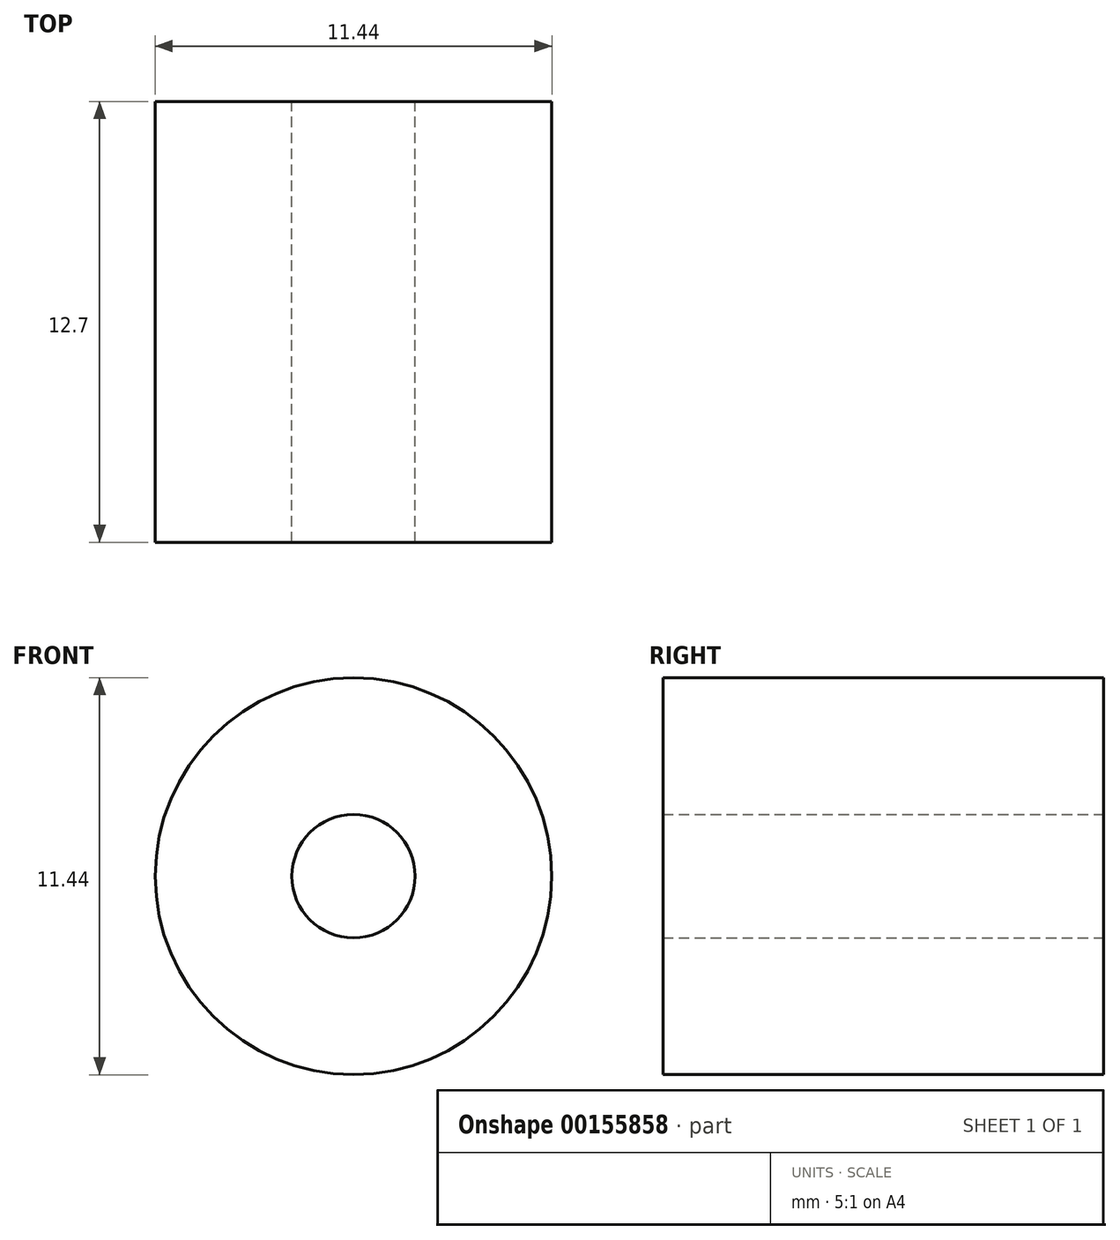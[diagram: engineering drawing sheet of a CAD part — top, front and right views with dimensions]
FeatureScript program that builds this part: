
annotation { "Feature Type Name" : "Feature", "Feature Type Description" : "" }
export const myFeature = defineFeature(function(context is Context, id is Id, definition is map)
    precondition{}
    {
        {
            var Q0;
            Q0=qCreatedBy(makeId("Front.planeOp"),FACE);
            var sketch = newSketch(context, id + "F0", { "sketchPlane" : qUnion([Q0])});
            skCircle(sketch, "E0", {"center": v(0, 0) * mm, "radius": 1.78 * mm});
            skCircle(sketch, "E1", {"center": v(0, 0) * mm, "radius": 5.72 * mm});
            skSolve(sketch);
        }
        {
            var Q0;
            Q0=makeQuery(id+"F0.imprint","IMPRINT",FACE,{"disambiguationData":[TD([[makeQuery(id+"F0.imprint","IMPRINT",EDGE,{"derivedFrom":sQuery(id+"F0.wireOp",EDGE,"E0")}),-1.0]])]});
            extrude(context, id + "F1", {"entities" : qUnion([Q0]), "depth" : 12.7 * mm});
        }
    });
